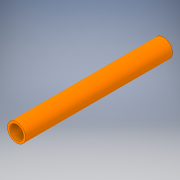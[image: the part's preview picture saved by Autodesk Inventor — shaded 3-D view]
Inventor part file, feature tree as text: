
AUTODESK INVENTOR PART (.ipt)
format: ipt  version: 2018.2 (Build 222227000, 227)  size: 108,544 bytes
history: native  units: in
note: dims shown in document units (in); Inventor stores cm internally (conversion verified against a paired STEP export)
features: extrude x1, sketch x1
ambient origin geometry x8: Origin, YZ Plane, XZ Plane, XY Plane, X Axis, Y Axis, Z Axis, Center Point
bodies: Solid1 (feature_tree)
feature tree (2):
  extrude  "Extrusion1"  Depth=10.584in
  sketch  "Sketch1"  dims[d0=1.315in d1=1.0in d2=10.584in d3=0.0in]
